# Revit family: 1990081 - Ronda ROG610-41 - Polar White
name_source: partatom
category: Plumbing Fixtures
units: mm (PartAtom-declared; Revit-internal decimal feet)

## family parameters
Always vertical = Yes
Cut with Voids When Loaded = No
OmniClass Number = 23.45.05.14.14
OmniClass Title = Sinks/Lavatories
Part Type = Normal
Room Calculation Point = No
Round Connector Dimension = Use Diameter
Shared = No
Work Plane-Based = No

## types (1)
- Rondo ROG610-41
    Assembly Code = D2010410
    Bowl Depth = 210 mm  [stored 0.688976 ft]
    Bowl Diameter = 400 mm  [stored 1.31234 ft]
    CW Connection = Yes
    Default Elevation = 0 mm  [stored 0 ft]
    Diameter = 510 mm  [stored 1.67323 ft]
    HW Connection = Yes
    Manufacturer = Franke South Africa (Pty) Ltd
    Material = Polar White
    Model = Rondo ROG610-41
    Product Code = 1990081
    Vent Connection = No
    Waste Connection = Yes

note: [stored X ft] marks values corroborated as IEEE doubles in the binary element streams (Revit-internal decimal feet)

## geometry (parser evidence)
native form markers: Blend x6, Sweep x3
no freeform markers — native parametric forms only
